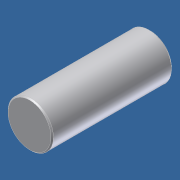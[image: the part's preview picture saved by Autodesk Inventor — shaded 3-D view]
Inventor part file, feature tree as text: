
AUTODESK INVENTOR PART (.ipt)
format: ipt  version: unknown  size: 169,472 bytes
history: native  units: in
note: dims shown in document units (in); Inventor stores cm internally (conversion verified against a paired STEP export)
features: other x35, revolve x1, sketch x1
ambient origin geometry x8: Origin, YZ Plane, XZ Plane, XY Plane, X Axis, Y Axis, Z Axis, Center Point
feature tree (37):
  revolve  "Revolution1"  [1 undecoded]
  other  "dia1_XY"
  other  "dia1_YZ"
  other  "dia1_ZX"
  other  "dia1_X"
  other  "dia1_Y"
  other  "dia1_Z"
  other  "dia1_Center"
  other  "dia2_XY"
  other  "dia2_YZ"
  other  "dia2_ZX"
  other  "dia2_X"
  other  "dia2_Y"
  other  "dia2_Z"
  other  "dia2_Center"
  other  "pin_XY"
  other  "pin_YZ"
  other  "pin_ZX"
  other  "pin_X"
  other  "pin_Y"
  other  "pin_Z"
  other  "pin_Center"
  other  "pin1_XY"
  other  "pin1_YZ"
  other  "pin1_ZX"
  other  "pin1_X"
  other  "pin1_Y"
  other  "pin1_Z"
  other  "pin1_Center"
  other  "pin2_XY"
  other  "pin2_YZ"
  other  "pin2_ZX"
  other  "pin2_X"
  other  "pin2_Y"
  other  "pin2_Z"
  other  "pin2_Center"
  sketch  "Sketch_1"  dims[d0=360.0deg]
note: 1 required parameter value undecoded (feature->parameter linkage not recoverable at this tier; creation-order binding heuristic only, values carry confidence <= 0.55)
